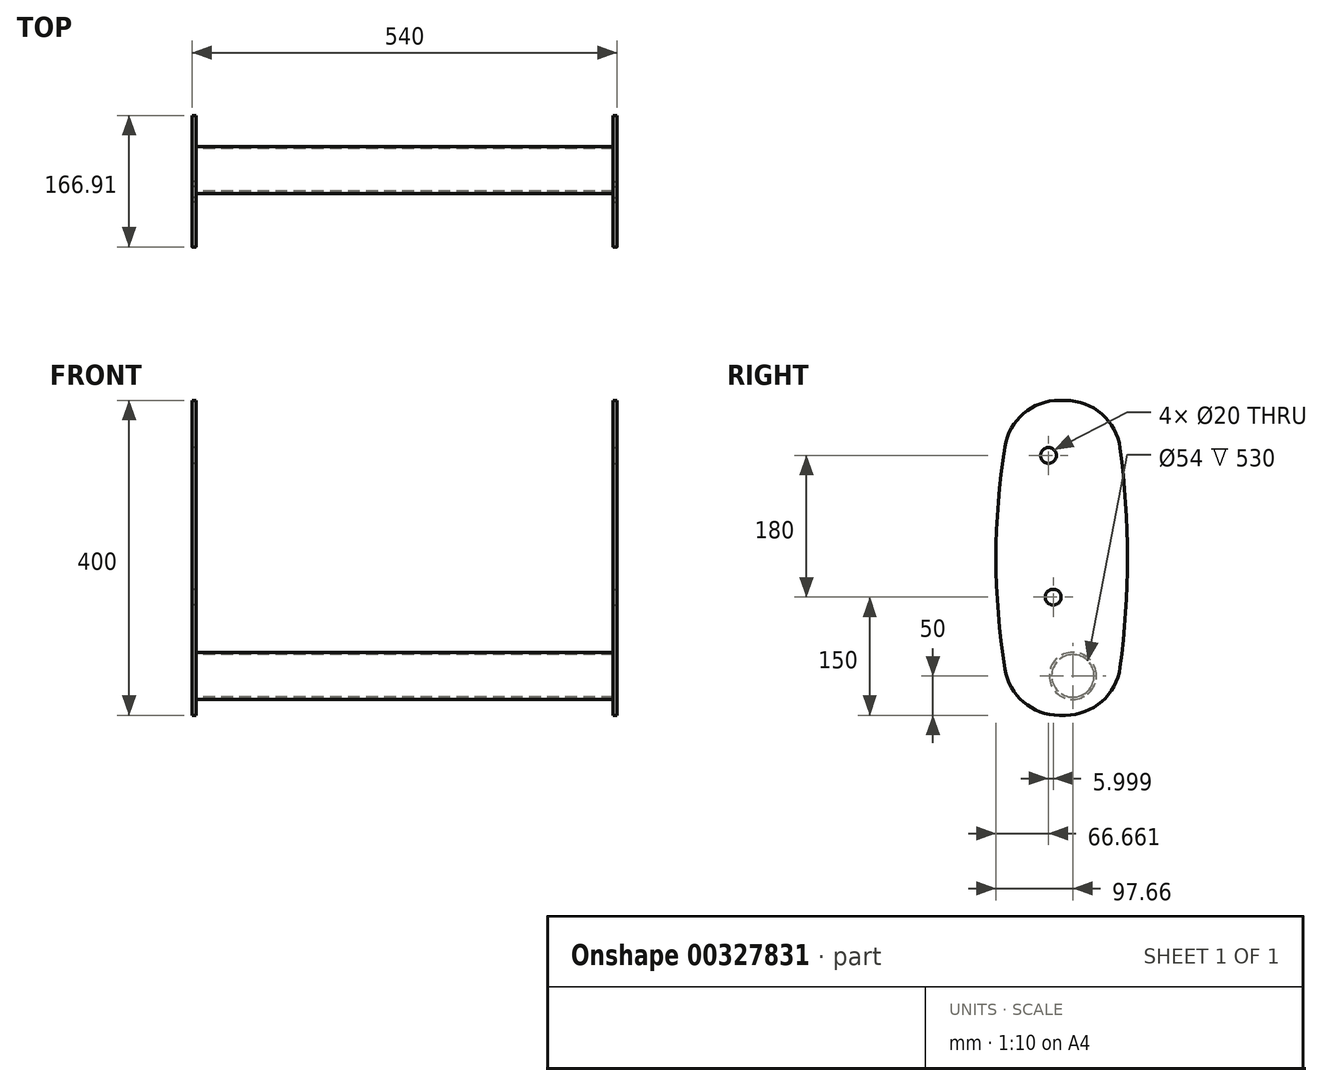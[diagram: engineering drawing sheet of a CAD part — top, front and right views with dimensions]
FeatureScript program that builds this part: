
annotation { "Feature Type Name" : "Feature", "Feature Type Description" : "" }
export const myFeature = defineFeature(function(context is Context, id is Id, definition is map)
    precondition{}
    {
        {
            var Q0;
            Q0=qCreatedBy(makeId("Right.planeOp"),FACE);
            var sketch = newSketch(context, id + "F0", { "sketchPlane" : qUnion([Q0])});
            skLineSegment(sketch, "E0.bottom", {"start": v(0, 100) * mm, "end": v(125, 100) * mm});
            skLineSegment(sketch, "E0.top", {"start": v(0, 500) * mm, "end": v(125, 500) * mm});
            skLineSegment(sketch, "E0.left", {"start": v(0, 100) * mm, "end": v(0, 500) * mm, "construction": true});
            skLineSegment(sketch, "E0.right", {"start": v(125, 100) * mm, "end": v(125, 500) * mm, "construction": true});
            skCircle(sketch, "E1", {"center": v(50, 250) * mm, "radius": 10 * mm});
            skCircle(sketch, "E2", {"center": v(44, 430) * mm, "radius": 10 * mm});
            skArc(sketch, "E3", {"start": v(0, 500) * mm, "mid": v(-22.66, 300) * mm, "end": v(0, 100) * mm});
            skArc(sketch, "E4", {"start": v(125, 100) * mm, "mid": v(144.25, 300) * mm, "end": v(125, 500) * mm});
            skCircle(sketch, "E5", {"center": v(75, 150) * mm, "radius": 30 * mm});
            skCircle(sketch, "E6", {"center": v(75, 150) * mm, "radius": 27 * mm});
            skSolve(sketch);
        }
        {
            var Q0;
            Q0=qCreatedBy(makeId("Right.planeOp"),FACE);
            cPlane(context, id + "F1", {"entities" : qUnion([Q0]), "cplaneType" : CPlaneType.OFFSET, "offset" : (530 / 2) * mm, "width" : 150 * mm, "height" : 150 * mm});
        }
        {
            var Q0;
            Q0=qCreatedBy(id+"F1.planeOp",FACE);
            var sketch = newSketch(context, id + "F2", { "sketchPlane" : qUnion([Q0])});
            skArc(sketch, "E7.0", {"start": v(0, 500) * mm, "mid": v(-22.66, 300) * mm, "end": v(0, 100) * mm});
            skLineSegment(sketch, "E7.1", {"start": v(0, 500) * mm, "end": v(125, 500) * mm});
            skArc(sketch, "E7.2", {"start": v(125, 100) * mm, "mid": v(144.25, 300) * mm, "end": v(125, 500) * mm});
            skLineSegment(sketch, "E7.3", {"start": v(0, 100) * mm, "end": v(125, 100) * mm});
            skSolve(sketch);
        }
        {
            var Q0;
            Q0 = qSketchRegion(id + "F2", true);
            extrude(context, id + "F3", {"entities" : qUnion([Q0]), "depth" : 5 * mm});
        }
        {
            var Q0;
            Q0=makeQuery(id+"F3.opExtrude","SWEPT_EDGE",EDGE,{"disambiguationData":[OSD([sQuery(id+"F2.wireOp",EDGE,"E7.0"),sQuery(id+"F2.wireOp",EDGE,"E7.1")])]});
            var Q1;
            Q1=makeQuery(id+"F3.opExtrude","SWEPT_EDGE",EDGE,{"disambiguationData":[OSD([sQuery(id+"F2.wireOp",EDGE,"E7.1"),sQuery(id+"F2.wireOp",EDGE,"E7.2")])]});
            var Q2;
            Q2=makeQuery(id+"F3.opExtrude","SWEPT_EDGE",EDGE,{"disambiguationData":[OSD([sQuery(id+"F2.wireOp",EDGE,"E7.0"),sQuery(id+"F2.wireOp",EDGE,"E7.3")])]});
            var Q3;
            Q3=makeQuery(id+"F3.opExtrude","SWEPT_EDGE",EDGE,{"disambiguationData":[OSD([sQuery(id+"F2.wireOp",EDGE,"E7.2"),sQuery(id+"F2.wireOp",EDGE,"E7.3")])]});
            fillet(context, id + "F4", {"entities" : qUnion([Q0, Q1, Q2, Q3]), "radius" : 70 * mm, "tangentPropagation" : true, "allowEdgeOverflow" : false});
        }
        {
            var Q0;
            Q0=makeQuery(id+"F3.opExtrude","CAP_FACE",FACE,{"disambiguationData":[OSD([sQuery(id+"F2.wireOp",EDGE,"E7.0"),sQuery(id+"F2.wireOp",EDGE,"E7.1"),sQuery(id+"F2.wireOp",EDGE,"E7.2"),sQuery(id+"F2.wireOp",EDGE,"E7.3")])],"isStart":false});
            var sketch = newSketch(context, id + "F5", { "sketchPlane" : qUnion([Q0])});
            skCircle(sketch, "E8.0", {"center": v(44, 430) * mm, "radius": 10 * mm});
            skCircle(sketch, "E8.1", {"center": v(50, 250) * mm, "radius": 10 * mm});
            skSolve(sketch);
        }
        {
            var Q0;
            Q0 = qSketchRegion(id + "F5", true);
            extrude(context, id + "F6", {"entities" : qUnion([Q0]), "operationType" : NewBodyOperationType.REMOVE, "endBound" : BoundingType.UP_TO_NEXT, "oppositeDirection" : true, "depth" : 25 * mm});
        }
        {
            var Q0;
            Q0=makeQuery(id+"F3.opExtrude","SWEPT_BODY",BODY,{"disambiguationData":[OSD([sQuery(id+"F2.wireOp",EDGE,"E7.0"),sQuery(id+"F2.wireOp",EDGE,"E7.1"),sQuery(id+"F2.wireOp",EDGE,"E7.2"),sQuery(id+"F2.wireOp",EDGE,"E7.3")])]});
            var Q1;
            Q1=qCreatedBy(makeId("Right.planeOp"),FACE);
            mirror(context, id + "F7", {"entities" : qUnion([Q0]), "mirrorPlane" : qUnion([Q1])});
        }
        {
            var Q0;
            Q0=makeQuery(id+"F0.imprint","IMPRINT",FACE,{"disambiguationData":[TD([[makeQuery(id+"F0.imprint","IMPRINT",EDGE,{"derivedFrom":sQuery(id+"F0.wireOp",EDGE,"E5")}),1.0]])]});
            var Q1;
            Q1=makeQuery(id+"F3.opExtrude","CAP_FACE",FACE,{"disambiguationData":[OSD([sQuery(id+"F2.wireOp",EDGE,"E7.0"),sQuery(id+"F2.wireOp",EDGE,"E7.1"),sQuery(id+"F2.wireOp",EDGE,"E7.2"),sQuery(id+"F2.wireOp",EDGE,"E7.3")])],"isStart":true});
            var Q2;
            Q2=makeQuery(id+"F7.opPattern","COPY",FACE,{"derivedFrom":makeQuery(id+"F3.opExtrude","CAP_FACE",FACE,{"disambiguationData":[OSD([sQuery(id+"F2.wireOp",EDGE,"E7.0"),sQuery(id+"F2.wireOp",EDGE,"E7.1"),sQuery(id+"F2.wireOp",EDGE,"E7.2"),sQuery(id+"F2.wireOp",EDGE,"E7.3")])],"isStart":true}),"instanceName":"1"});
            extrude(context, id + "F8", {"entities" : qUnion([Q0]), "endBound" : BoundingType.UP_TO_SURFACE, "endBoundEntityFace" : qUnion([Q1]), "depth" : 25 * mm, "hasSecondDirection" : true, "secondDirectionBound" : SecondDirectionBoundingType.UP_TO_SURFACE, "secondDirectionOppositeDirection" : true, "secondDirectionBoundEntityFace" : qUnion([Q2]), "secondDirectionDepth" : 25 * mm});
        }
    });
